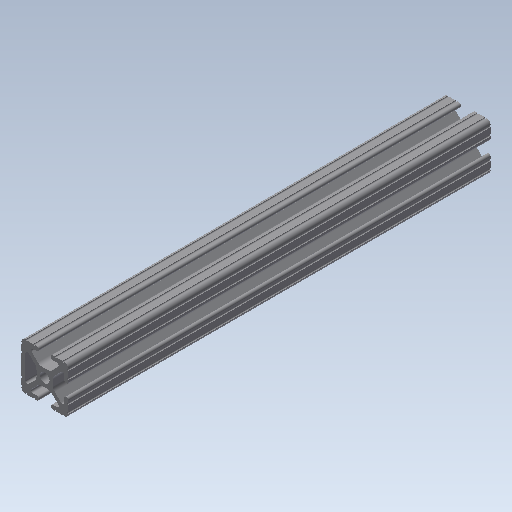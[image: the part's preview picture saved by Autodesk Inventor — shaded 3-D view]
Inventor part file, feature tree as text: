
AUTODESK INVENTOR PART (.ipt)
format: ipt  version: 2020 (Build 240168000, 168)  size: 224,768 bytes
history: native  units: in
note: dims shown in document units (in); Inventor stores cm internally (conversion verified against a paired STEP export)
features: extrude x1, sketch x1
ambient origin geometry x8: Origin, YZ Plane, XZ Plane, XY Plane, X Axis, Y Axis, Z Axis, Center Point
bodies: Solid1 (feature_tree)
feature tree (2):
  extrude  "Extrusion1"  [1 undecoded]
  sketch  "Sketch_1"  dims[d0=9.0in d1=0.0in]
note: 1 required parameter value undecoded (feature->parameter linkage not recoverable at this tier; creation-order binding heuristic only, values carry confidence <= 0.55)
